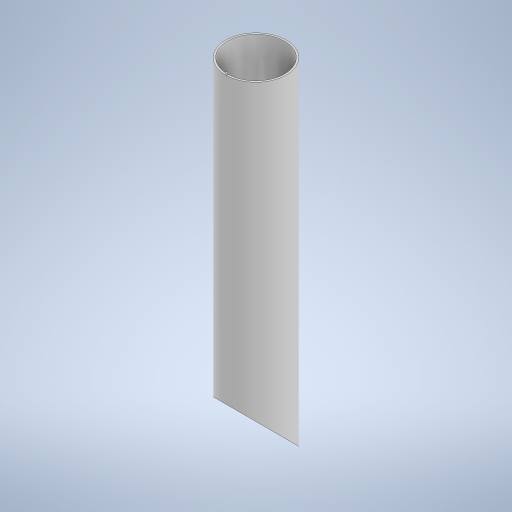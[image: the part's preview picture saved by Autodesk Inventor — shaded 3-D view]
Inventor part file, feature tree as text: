
AUTODESK INVENTOR PART (.ipt)
format: ipt  version: 2024.3 (Build 283343000, 343)  size: 250,368 bytes
history: native  units: mm
features: extrude x3, sketch x3
ambient origin geometry x8: Origin, YZ Plane, XZ Plane, XY Plane, X Axis, Y Axis, Z Axis, Center Point
bodies: Solid1 (feature_tree)
feature tree (6):
  extrude  "Extrusion1"  Depth=2.0mm
  extrude  "Extrusion2"  Depth=400.0mm
  extrude  "Extrusion4"  Depth=2.0mm TaperAngle=0.0deg
  sketch  "Sketch1"  dims[d0=2.0mm d1=70.0mm]
  sketch  "Sketch2"  dims[d2=400.0mm d3=0.0mm d4=70.0mm]
  sketch  "Sketch4"  dims[d5=0.0mm d6=0.0mm d9=2.0mm d10=0.0mm]
